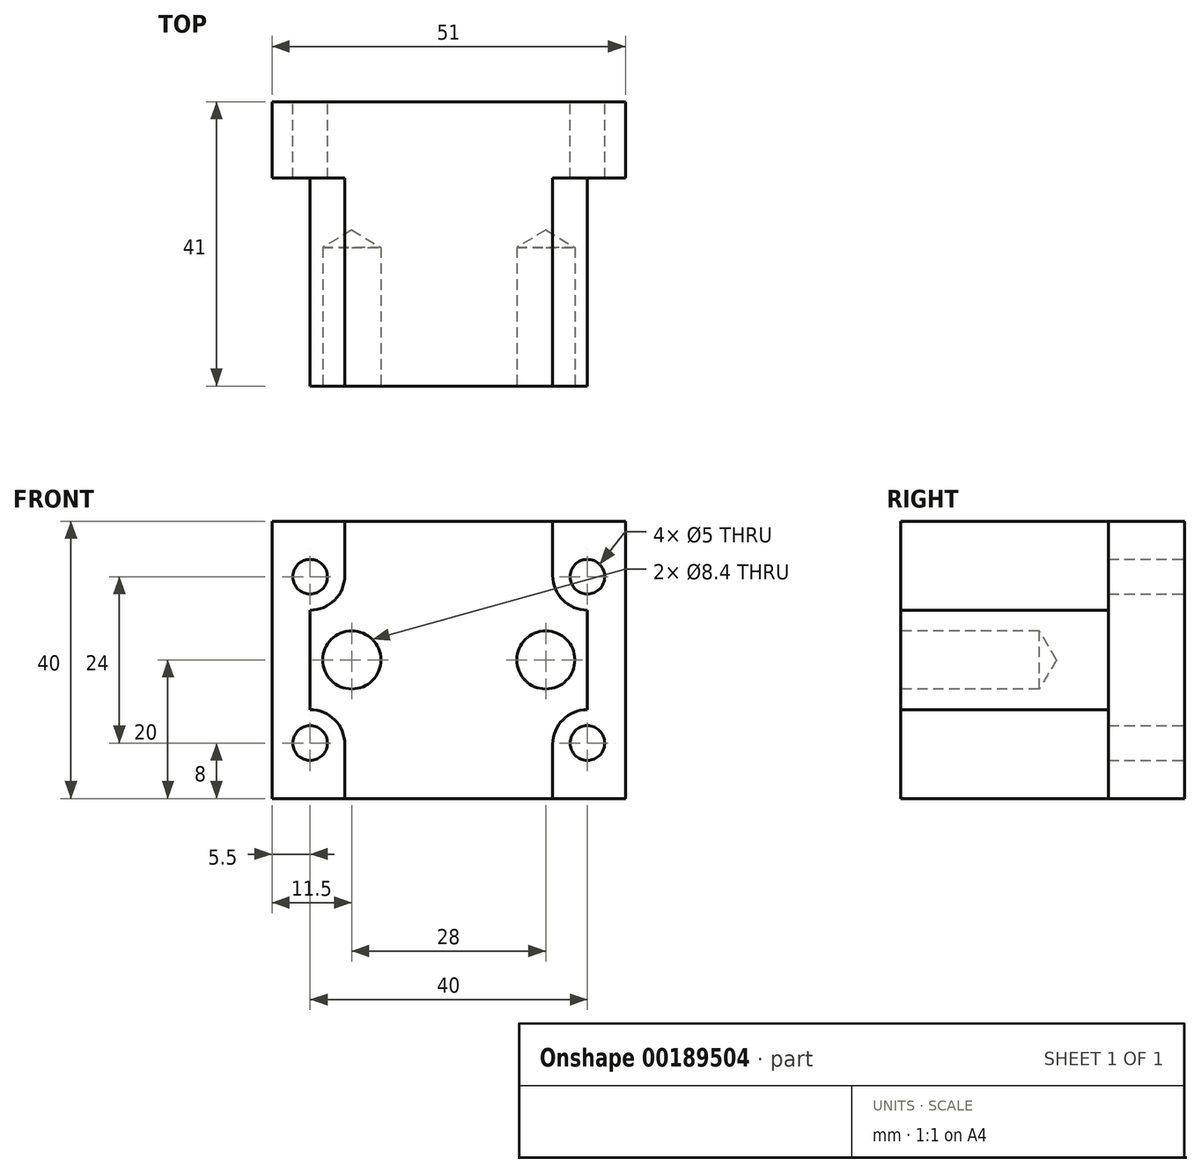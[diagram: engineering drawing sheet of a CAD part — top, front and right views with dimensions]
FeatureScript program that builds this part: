
annotation { "Feature Type Name" : "Feature", "Feature Type Description" : "" }
export const myFeature = defineFeature(function(context is Context, id is Id, definition is map)
    precondition{}
    {
        {
            var Q0;
            Q0=qCreatedBy(makeId("Front.planeOp"),FACE);
            var sketch = newSketch(context, id + "F0", { "sketchPlane" : qUnion([Q0])});
            skLineSegment(sketch, "E0.bottom", {"start": v(25.5, 20) * mm, "end": v(-25.5, 20) * mm});
            skLineSegment(sketch, "E0.top", {"start": v(25.5, -20) * mm, "end": v(-25.5, -20) * mm});
            skLineSegment(sketch, "E0.left", {"start": v(25.5, 20) * mm, "end": v(25.5, -20) * mm});
            skLineSegment(sketch, "E0.right", {"start": v(-25.5, 20) * mm, "end": v(-25.5, -20) * mm});
            skPoint(sketch, "E0.middle", {"position": v(0, 0) * mm});
            skSolve(sketch);
        }
        {
            var Q0;
            Q0 = qSketchRegion(id + "F0", true);
            extrude(context, id + "F1", {"entities" : qUnion([Q0]), "depth" : 41 * mm});
        }
        {
            var Q0;
            Q0=makeQuery(id+"F1.opExtrude","CAP_FACE",FACE,{"disambiguationData":[OSD([sQuery(id+"F0.wireOp",EDGE,"E0.bottom"),sQuery(id+"F0.wireOp",EDGE,"E0.top"),sQuery(id+"F0.wireOp",EDGE,"E0.left"),sQuery(id+"F0.wireOp",EDGE,"E0.right")])],"isStart":true});
            var sketch = newSketch(context, id + "F2", { "sketchPlane" : qUnion([Q0])});
            skCircle(sketch, "E1", {"center": v(-20, 12) * mm, "radius": 2.5 * mm});
            skCircle(sketch, "E2", {"center": v(-20, -12) * mm, "radius": 2.5 * mm});
            skCircle(sketch, "E3.MirrorC", {"center": v(20, -12) * mm, "radius": 2.5 * mm});
            skCircle(sketch, "E4.MirrorC", {"center": v(20, 12) * mm, "radius": 2.5 * mm});
            skSolve(sketch);
        }
        {
            var Q0;
            Q0=makeQuery(id+"F1.opExtrude","CAP_FACE",FACE,{"disambiguationData":[OSD([sQuery(id+"F0.wireOp",EDGE,"E0.bottom"),sQuery(id+"F0.wireOp",EDGE,"E0.top"),sQuery(id+"F0.wireOp",EDGE,"E0.left"),sQuery(id+"F0.wireOp",EDGE,"E0.right")])],"isStart":false});
            var sketch = newSketch(context, id + "F3", { "sketchPlane" : qUnion([Q0])});
            skCircle(sketch, "E5", {"center": v(-14, 0) * mm, "radius": 4 * mm});
            skCircle(sketch, "E6", {"center": v(14, 0) * mm, "radius": 4 * mm});
            skSolve(sketch);
        }
        {
            var Q0;
            Q0=makeQuery(id+"F3.imprint","IMPRINT",FACE,{"disambiguationData":[TD([[makeQuery(id+"F3.imprint","IMPRINT",EDGE,{"derivedFrom":sQuery(id+"F3.wireOp",EDGE,"E5")}),-1.0]])]});
            var sketch = newSketch(context, id + "F4", { "sketchPlane" : qUnion([Q0])});
            skLineSegment(sketch, "E7.left", {"start": v(20, 20) * mm, "end": v(20, -20) * mm});
            skPoint(sketch, "E7.middle", {"position": v(0, 0) * mm});
            skLineSegment(sketch, "E8", {"start": v(20, 20) * mm, "end": v(25.5, 20) * mm});
            skLineSegment(sketch, "E9", {"start": v(25.5, 20) * mm, "end": v(25.5, -20) * mm});
            skLineSegment(sketch, "E10", {"start": v(25.5, -20) * mm, "end": v(20, -20) * mm});
            skPoint(sketch, "E7.right.start.orphan", {"position": v(-20, 20) * mm});
            skPoint(sketch, "E7.top.end.orphan", {"position": v(-20, -20) * mm});
            skLineSegment(sketch, "E11.MirrorCS", {"start": v(-20, 20) * mm, "end": v(-25.5, 20) * mm});
            skLineSegment(sketch, "E12.MirrorCS", {"start": v(-25.5, -20) * mm, "end": v(-20, -20) * mm});
            skLineSegment(sketch, "E13.MirrorCS", {"start": v(-20, 20) * mm, "end": v(-20, -20) * mm});
            skLineSegment(sketch, "E14.MirrorCS", {"start": v(-25.5, 20) * mm, "end": v(-25.5, -20) * mm});
            skSolve(sketch);
        }
        {
            var Q0;
            Q0 = qSketchRegion(id + "F4", true);
            extrude(context, id + "F5", {"entities" : qUnion([Q0]), "operationType" : NewBodyOperationType.REMOVE, "oppositeDirection" : true, "depth" : 30 * mm});
        }
        {
            var Q0;
            Q0=makeQuery(id+"F3.imprint","IMPRINT",FACE,{"disambiguationData":[TD([[makeQuery(id+"F3.imprint","IMPRINT",EDGE,{"derivedFrom":sQuery(id+"F3.wireOp",EDGE,"E5")}),-1.0]])]});
            var sketch = newSketch(context, id + "F6", { "sketchPlane" : qUnion([Q0])});
            skArc(sketch, "E15", {"start": v(-20, 17.17) * mm, "mid": v(-23.54, 8.64) * mm, "end": v(-15, 12.17) * mm});
            skPoint(sketch, "E16.0", {"position": v(-20, 20) * mm});
            skLineSegment(sketch, "E17", {"start": v(-20, 17.17) * mm, "end": v(-20, 20) * mm});
            skLineSegment(sketch, "E18", {"start": v(-20, 20) * mm, "end": v(-15, 20) * mm});
            skLineSegment(sketch, "E19", {"start": v(-15, 12.17) * mm, "end": v(-15, 20) * mm});
            skLineSegment(sketch, "E20.MirrorCS", {"start": v(20, 20) * mm, "end": v(15, 20) * mm});
            skPoint(sketch, "E21.MirrorP", {"position": v(20, 20) * mm});
            skArc(sketch, "E22.MirrorCS", {"start": v(20, 17.17) * mm, "mid": v(23.54, 8.64) * mm, "end": v(15, 12.17) * mm});
            skLineSegment(sketch, "E23.MirrorCS", {"start": v(20, 17.17) * mm, "end": v(20, 20) * mm});
            skLineSegment(sketch, "E24.MirrorCS", {"start": v(15, 12.17) * mm, "end": v(15, 20) * mm});
            skLineSegment(sketch, "E25.MirrorCS", {"start": v(20, -17.17) * mm, "end": v(20, -20) * mm});
            skLineSegment(sketch, "E26.MirrorCS", {"start": v(-20, -17.17) * mm, "end": v(-20, -20) * mm});
            skLineSegment(sketch, "E27.MirrorCS", {"start": v(15, -12.17) * mm, "end": v(15, -20) * mm});
            skArc(sketch, "E28.MirrorCS", {"start": v(20, -17.17) * mm, "mid": v(23.54, -8.64) * mm, "end": v(15, -12.17) * mm});
            skLineSegment(sketch, "E29.MirrorCS", {"start": v(20, -20) * mm, "end": v(15, -20) * mm});
            skArc(sketch, "E30.MirrorCS", {"start": v(-20, -17.17) * mm, "mid": v(-23.54, -8.64) * mm, "end": v(-15, -12.17) * mm});
            skPoint(sketch, "E31.MirrorP", {"position": v(20, -20) * mm});
            skLineSegment(sketch, "E32.MirrorCS", {"start": v(-20, -20) * mm, "end": v(-15, -20) * mm});
            skLineSegment(sketch, "E33.MirrorCS", {"start": v(-15, -12.17) * mm, "end": v(-15, -20) * mm});
            skPoint(sketch, "E34.MirrorP", {"position": v(-20, -20) * mm});
            skSolve(sketch);
        }
        {
            var Q0;
            Q0 = qSketchRegion(id + "F6", true);
            extrude(context, id + "F7", {"entities" : qUnion([Q0]), "operationType" : NewBodyOperationType.REMOVE, "oppositeDirection" : true, "depth" : 30 * mm});
        }
        {
            var Q0;
            Q0 = qSketchRegion(id + "F2", true);
            extrude(context, id + "F8", {"entities" : qUnion([Q0]), "operationType" : NewBodyOperationType.REMOVE, "endBound" : BoundingType.THROUGH_ALL, "oppositeDirection" : true, "depth" : 25 * mm});
        }
        {
            var Q0;
            Q0=sQuery(id+"F3.wireOp",VERTEX,"E5.center");
            var Q1;
            Q1=sQuery(id+"F3.wireOp",VERTEX,"E6.center");
            var Q2;
            Q2=makeQuery(id+"F1.opExtrude","SWEPT_BODY",BODY,{"disambiguationData":[OSD([sQuery(id+"F0.wireOp",EDGE,"E0.bottom"),sQuery(id+"F0.wireOp",EDGE,"E0.top"),sQuery(id+"F0.wireOp",EDGE,"E0.left"),sQuery(id+"F0.wireOp",EDGE,"E0.right")])]});
            hole(context, id + "F9", {"style" : HoleStyle.SIMPLE, "endStyle" : HoleEndStyle.BLIND, "standardTappedOrClearance" : lookupTablePath({ "standard" : "ISO", "fit" : "Close", "size" : "M8", "type" : "Clearance" }), "standardBlindInLast" : lookupTablePath({ "fit" : "Close", "standard" : "ISO", "size" : "M8", "type" : "Clearance" }), "holeDiameter" : 8.4 * mm, "holeDepth" : 20 * mm, "locations" : qUnion([Q0, Q1]), "scope" : qUnion([Q2])});
        }
    });
